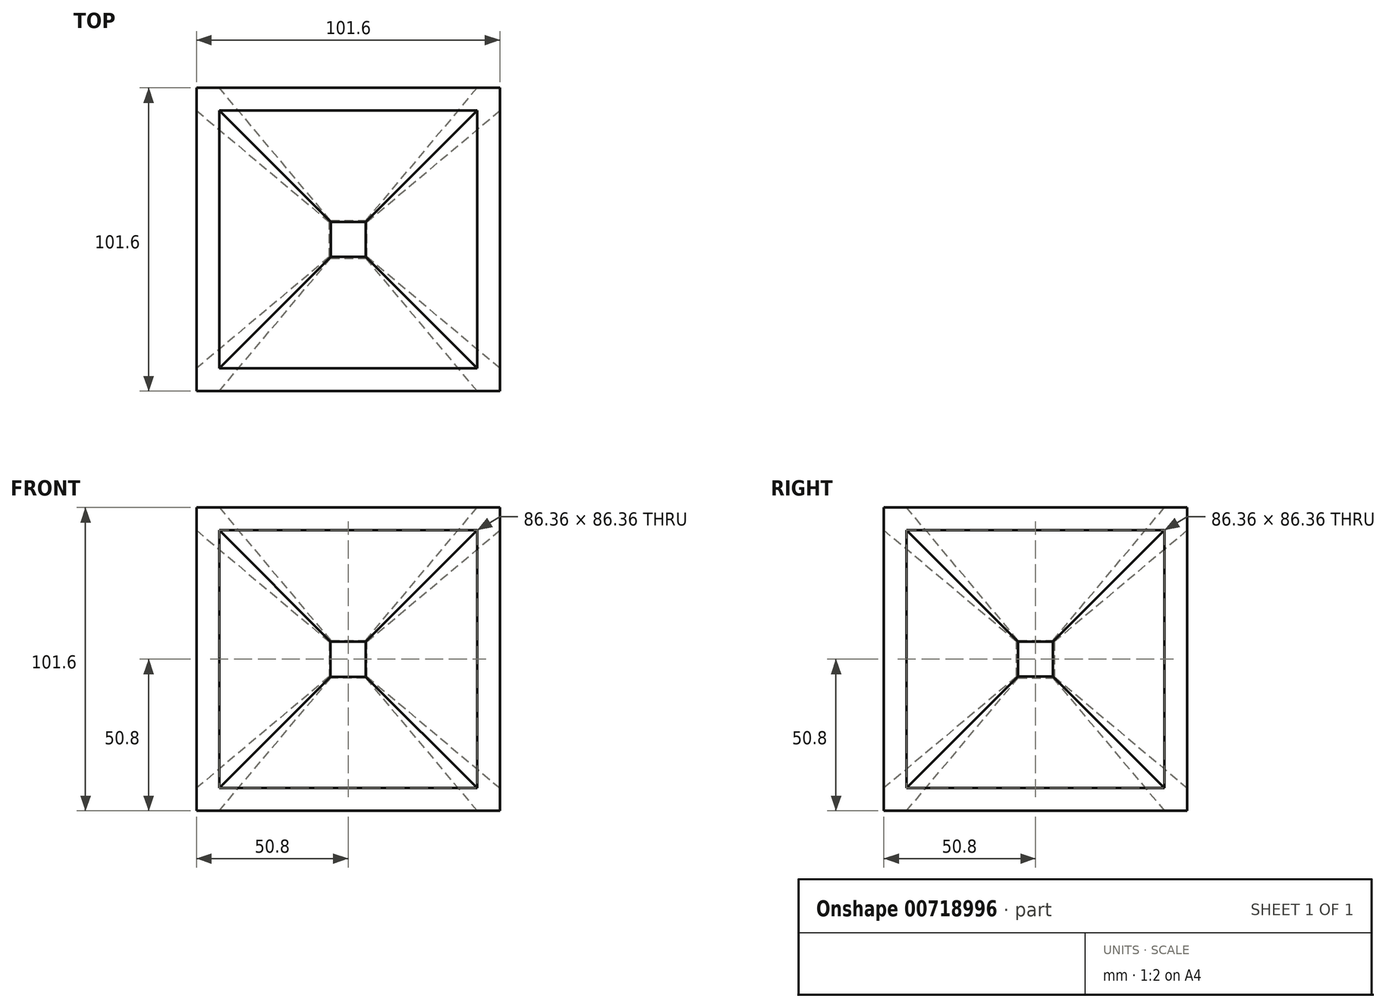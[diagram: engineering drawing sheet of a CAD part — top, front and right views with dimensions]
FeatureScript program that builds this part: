
annotation { "Feature Type Name" : "Feature", "Feature Type Description" : "" }
export const myFeature = defineFeature(function(context is Context, id is Id, definition is map)
    precondition{}
    {
        {
            var Q0;
            Q0=qCreatedBy(makeId("Top.planeOp"),FACE);
            var sketch = newSketch(context, id + "F0", { "sketchPlane" : qUnion([Q0])});
            skLineSegment(sketch, "E0.bottom", {"start": v(0, 0) * mm, "end": v(-101.6, 0) * mm});
            skLineSegment(sketch, "E0.top", {"start": v(0, 101.6) * mm, "end": v(-101.6, 101.6) * mm});
            skLineSegment(sketch, "E0.left", {"start": v(0, 0) * mm, "end": v(0, 101.6) * mm});
            skLineSegment(sketch, "E0.right", {"start": v(-101.6, 0) * mm, "end": v(-101.6, 101.6) * mm});
            skSolve(sketch);
        }
        {
            var Q0;
            Q0 = qSketchRegion(id + "F0", true);
            extrude(context, id + "F1", {"entities" : qUnion([Q0]), "depth" : 101.6 * mm, "offsetDistance" : 25.4 * mm});
        }
        {
            var Q0;
            Q0=makeQuery(id+"F1.opExtrude","SWEPT_FACE",FACE,{"disambiguationData":[OSD([sQuery(id+"F0.wireOp",EDGE,"E0.bottom")])]});
            var sketch = newSketch(context, id + "F2", { "sketchPlane" : qUnion([Q0])});
            skLineSegment(sketch, "E1.bottom", {"start": v(-93.98, 93.98) * mm, "end": v(-7.62, 93.98) * mm});
            skLineSegment(sketch, "E1.top", {"start": v(-93.98, 7.62) * mm, "end": v(-7.62, 7.62) * mm});
            skLineSegment(sketch, "E1.left", {"start": v(-93.98, 93.98) * mm, "end": v(-93.98, 7.62) * mm});
            skLineSegment(sketch, "E1.right", {"start": v(-7.62, 93.98) * mm, "end": v(-7.62, 7.62) * mm});
            skSolve(sketch);
        }
        {
            var Q0;
            Q0 = qSketchRegion(id + "F2", true);
            extrude(context, id + "F3", {"entities" : qUnion([Q0]), "operationType" : NewBodyOperationType.REMOVE, "oppositeDirection" : true, "depth" : 47 * mm, "offsetDistance" : 25.4 * mm, "hasDraft" : true, "draftAngle" : 40 * degree, "draftPullDirection" : true});
        }
        {
            var Q0;
            Q0=makeQuery(id+"F1.opExtrude","SWEPT_FACE",FACE,{"disambiguationData":[OSD([sQuery(id+"F0.wireOp",EDGE,"E0.left")])]});
            var sketch = newSketch(context, id + "F4", { "sketchPlane" : qUnion([Q0])});
            skLineSegment(sketch, "E2.bottom", {"start": v(7.62, 93.98) * mm, "end": v(93.98, 93.98) * mm});
            skLineSegment(sketch, "E2.top", {"start": v(7.62, 7.62) * mm, "end": v(93.98, 7.62) * mm});
            skLineSegment(sketch, "E2.left", {"start": v(7.62, 93.98) * mm, "end": v(7.62, 7.62) * mm});
            skLineSegment(sketch, "E2.right", {"start": v(93.98, 93.98) * mm, "end": v(93.98, 7.62) * mm});
            skSolve(sketch);
        }
        {
            var Q0;
            Q0 = qSketchRegion(id + "F4", true);
            extrude(context, id + "F5", {"entities" : qUnion([Q0]), "operationType" : NewBodyOperationType.REMOVE, "oppositeDirection" : true, "depth" : 47 * mm, "offsetDistance" : 25.4 * mm, "hasDraft" : true, "draftAngle" : 40 * degree, "draftPullDirection" : true});
        }
        {
            var Q0;
            Q0=makeQuery(id+"F1.opExtrude","CAP_FACE",FACE,{"disambiguationData":[OSD([sQuery(id+"F0.wireOp",EDGE,"E0.bottom"),sQuery(id+"F0.wireOp",EDGE,"E0.top"),sQuery(id+"F0.wireOp",EDGE,"E0.left"),sQuery(id+"F0.wireOp",EDGE,"E0.right")])],"isStart":false});
            var sketch = newSketch(context, id + "F6", { "sketchPlane" : qUnion([Q0])});
            skLineSegment(sketch, "E3.bottom", {"start": v(-93.98, 93.98) * mm, "end": v(-7.62, 93.98) * mm});
            skLineSegment(sketch, "E3.top", {"start": v(-93.98, 7.62) * mm, "end": v(-7.62, 7.62) * mm});
            skLineSegment(sketch, "E3.left", {"start": v(-93.98, 93.98) * mm, "end": v(-93.98, 7.62) * mm});
            skLineSegment(sketch, "E3.right", {"start": v(-7.62, 93.98) * mm, "end": v(-7.62, 7.62) * mm});
            skSolve(sketch);
        }
        {
            var Q0;
            Q0 = qSketchRegion(id + "F6", true);
            extrude(context, id + "F7", {"entities" : qUnion([Q0]), "operationType" : NewBodyOperationType.REMOVE, "oppositeDirection" : true, "depth" : 47 * mm, "offsetDistance" : 25.4 * mm, "hasDraft" : true, "draftAngle" : 40 * degree, "draftPullDirection" : true});
        }
        {
            var Q0;
            Q0=makeQuery(id+"F1.opExtrude","SWEPT_FACE",FACE,{"disambiguationData":[OSD([sQuery(id+"F0.wireOp",EDGE,"E0.right")])]});
            var sketch = newSketch(context, id + "F8", { "sketchPlane" : qUnion([Q0])});
            skLineSegment(sketch, "E4.bottom", {"start": v(-93.98, 93.98) * mm, "end": v(-7.62, 93.98) * mm});
            skLineSegment(sketch, "E4.top", {"start": v(-93.98, 7.62) * mm, "end": v(-7.62, 7.62) * mm});
            skLineSegment(sketch, "E4.left", {"start": v(-93.98, 93.98) * mm, "end": v(-93.98, 7.62) * mm});
            skLineSegment(sketch, "E4.right", {"start": v(-7.62, 93.98) * mm, "end": v(-7.62, 7.62) * mm});
            skSolve(sketch);
        }
        {
            var Q0;
            Q0 = qSketchRegion(id + "F8", true);
            extrude(context, id + "F9", {"entities" : qUnion([Q0]), "operationType" : NewBodyOperationType.REMOVE, "oppositeDirection" : true, "depth" : 47 * mm, "offsetDistance" : 25.4 * mm, "hasDraft" : true, "draftAngle" : 40 * degree, "draftPullDirection" : true});
        }
        {
            var Q0;
            Q0=makeQuery(id+"F1.opExtrude","SWEPT_FACE",FACE,{"disambiguationData":[OSD([sQuery(id+"F0.wireOp",EDGE,"E0.top")])]});
            var sketch = newSketch(context, id + "F10", { "sketchPlane" : qUnion([Q0])});
            skLineSegment(sketch, "E5.bottom", {"start": v(7.62, 93.98) * mm, "end": v(93.98, 93.98) * mm});
            skLineSegment(sketch, "E5.top", {"start": v(7.62, 7.62) * mm, "end": v(93.98, 7.62) * mm});
            skLineSegment(sketch, "E5.left", {"start": v(7.62, 93.98) * mm, "end": v(7.62, 7.62) * mm});
            skLineSegment(sketch, "E5.right", {"start": v(93.98, 93.98) * mm, "end": v(93.98, 7.62) * mm});
            skSolve(sketch);
        }
        {
            var Q0;
            Q0 = qSketchRegion(id + "F10", true);
            extrude(context, id + "F11", {"entities" : qUnion([Q0]), "operationType" : NewBodyOperationType.REMOVE, "oppositeDirection" : true, "depth" : 47 * mm, "offsetDistance" : 25.4 * mm, "hasDraft" : true, "draftAngle" : 40 * degree, "draftPullDirection" : true});
        }
        {
            var Q0;
            Q0=makeQuery(id+"F1.opExtrude","CAP_FACE",FACE,{"disambiguationData":[OSD([sQuery(id+"F0.wireOp",EDGE,"E0.bottom"),sQuery(id+"F0.wireOp",EDGE,"E0.top"),sQuery(id+"F0.wireOp",EDGE,"E0.left"),sQuery(id+"F0.wireOp",EDGE,"E0.right")])],"isStart":true});
            var sketch = newSketch(context, id + "F12", { "sketchPlane" : qUnion([Q0])});
            skLineSegment(sketch, "E6.bottom", {"start": v(-93.98, -7.62) * mm, "end": v(-7.62, -7.62) * mm});
            skLineSegment(sketch, "E6.top", {"start": v(-93.98, -93.98) * mm, "end": v(-7.62, -93.98) * mm});
            skLineSegment(sketch, "E6.left", {"start": v(-93.98, -7.62) * mm, "end": v(-93.98, -93.98) * mm});
            skLineSegment(sketch, "E6.right", {"start": v(-7.62, -7.62) * mm, "end": v(-7.62, -93.98) * mm});
            skSolve(sketch);
        }
        {
            var Q0;
            Q0 = qSketchRegion(id + "F12", true);
            extrude(context, id + "F13", {"entities" : qUnion([Q0]), "operationType" : NewBodyOperationType.REMOVE, "oppositeDirection" : true, "depth" : 47 * mm, "offsetDistance" : 25.4 * mm, "hasDraft" : true, "draftAngle" : 40 * degree, "draftPullDirection" : true});
        }
        {
            var Q0;
            Q0=makeQuery(id+"F3.boolean.opBoolean","COPY",FACE,{"derivedFrom":makeQuery(id+"F3.opExtrude","CAP_FACE",FACE,{"disambiguationData":[OSD([sQuery(id+"F2.wireOp",EDGE,"E1.bottom"),sQuery(id+"F2.wireOp",EDGE,"E1.top"),sQuery(id+"F2.wireOp",EDGE,"E1.left"),sQuery(id+"F2.wireOp",EDGE,"E1.right")])],"isStart":false})});
            var sketch = newSketch(context, id + "F14", { "sketchPlane" : qUnion([Q0])});
            skLineSegment(sketch, "E7.bottom", {"start": v(-57.1, 57.1) * mm, "end": v(-44.5, 57.1) * mm});
            skLineSegment(sketch, "E7.top", {"start": v(-57.1, 44.5) * mm, "end": v(-44.5, 44.5) * mm});
            skLineSegment(sketch, "E7.left", {"start": v(-57.1, 57.1) * mm, "end": v(-57.1, 44.5) * mm});
            skLineSegment(sketch, "E7.right", {"start": v(-44.5, 57.1) * mm, "end": v(-44.5, 44.5) * mm});
            skSolve(sketch);
        }
        {
            var Q0;
            Q0 = qSketchRegion(id + "F14", true);
            extrude(context, id + "F15", {"entities" : qUnion([Q0]), "operationType" : NewBodyOperationType.ADD, "depth" : 2.54 * mm, "offsetDistance" : 25.4 * mm, "hasSecondDirection" : true, "secondDirectionOppositeDirection" : true, "secondDirectionDepth" : 10.16 * mm});
        }
    });
